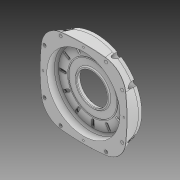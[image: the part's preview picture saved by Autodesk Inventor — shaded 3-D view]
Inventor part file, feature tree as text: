
AUTODESK INVENTOR PART (.ipt)
format: ipt  version: 2020 (Build 240168000, 168)  size: 960,000 bytes
history: native  units: mm
features: sketch x20, extrude x17, projected_geometry x5, other x4, plane x3, fillet x2, loft x1, revolve x1, pattern_circular x1, chamfer x1
ambient origin geometry x8: Origin, YZ Plane, XZ Plane, XY Plane, X Axis, Y Axis, Z Axis, Center Point
bodies: Solid1 (feature_tree)
feature tree (55):
  other  "Blocks"
  sketch  "Sketch1"  dims[d1=170.0mm d2=170.0mm]
  extrude  "Extrusion1"  Depth=170.0mm
  extrude  "Extrusion2"  Depth=60.0mm TaperAngle=0.0deg
  plane  "Work Plane1"
  loft  "Loft1"
  extrude  "Extrusion3"  Depth=7.5mm
  plane  "Work Plane2"
  sketch  "Sketch6"  dims[d14=17.5mm d15=7.5mm]
  plane  "Work Plane3"
  sketch  "Sketch7"  dims[d16=10.0mm d17=65.0mm]
  extrude  "Extrusion4"  Depth=7.5mm
  extrude  "Extrusion5"  Depth=7.5mm
  extrude  "Extrusion9"  Depth=10.0mm
  sketch  "Sketch13"  dims[d23=0.0mm d24=90.0deg d25=5.0mm d26=0.0mm]
  extrude  "Extrusion10"  Depth=7.5mm
  extrude  "Extrusion11"  TaperAngle=0.0deg  [1 undecoded]
  extrude  "Extrusion12"  Depth=5.0mm TaperAngle=0.0deg
  revolve  "Revolution1"  [1 undecoded]
  extrude  "Extrusion13"  Depth=4.0mm
  extrude  "Extrusion14"  Depth=10.0mm
  extrude  "Extrusion15"  Depth=6.0mm TaperAngle=0.0deg
  fillet  "Fillet1"  Radius=6.0mm
  extrude  "Extrusion16"  Depth=47.0mm
  fillet  "Fillet3"  Radius=60.0mm
  pattern_circular  "Circular Pattern1"  Count=6  [1 undecoded]
  extrude  "Extrusion17"  Depth=42.0mm
  extrude  "Extrusion18"  Depth=40.0mm
  extrude  "Extrusion19"  Depth=6.0mm
  extrude  "Extrusion20"  Depth=6.0mm TaperAngle=0.0deg
  chamfer  "Chamfer1"  Distance=7.0mm
  sketch  "Sketch2"  dims[d3=40.0mm d4=60.0mm d5=0.0mm]
  other  "Block1"
  sketch  "Sketch3"  dims[d7=0.0mm d8=0.0mm d9=5.5mm]
  sketch  "Sketch4"  dims[d10=57.5mm d11=7.5mm]
  projected_geometry  "Projected Loop1"
  sketch  "Sketch5"  dims[d12=7.5mm d13=7.5mm]
  projected_geometry  "Projected Loop2"
  projected_geometry  "Projected Loop3"
  projected_geometry  "Projected Loop4"
  sketch  "Sketch8"  dims[d18=7.5mm d19=7.5mm]
  sketch  "Sketch12"  dims[d20=25.0mm d21=0.0mm d22=90.0deg]
  projected_geometry  "Projected Loop5"
  sketch  "Sketch14"  dims[d27=180.0mm d28=-3.0mm]
  sketch  "Sketch15"  dims[d29=2.5mm d30=4.0mm]
  sketch  "Sketch16"  dims[d31=10.0mm d32=0.0mm d33=145.0mm]
  sketch  "Sketch17"  dims[d34=48.25mm d35=0.0mm d54=60.0mm d55=0.0mm d56=6.0mm d57=0.0mm]
  sketch  "Sketch18"  dims[d58=47.0mm d59=47.0mm d60=60.0mm d61=60.0mm]
  sketch  "Sketch19"  dims[d62=42.0mm d63=42.0mm]
  sketch  "Sketch20"  dims[d64=5.5mm d65=40.0mm]
  sketch  "Sketch21"  dims[d66=6.0mm d67=0.0mm d68=22.1mm]
  sketch  "Sketch22"  dims[d69=16.0mm d70=6.0mm d71=0.0mm]
  sketch  "Sketch23"  dims[d74=25.0mm d78=7.0mm d81=90.0deg d82=59.39697mm d83=10.0mm d85=6.2mm d86=9.0mm d87=40.0mm d89=360.0deg d91=48.25mm d92=0.0mm d93=9.0mm d94=40.0mm d96=360.0deg d98=20.0mm d99=0.0mm d100=0.0mm d101=0.0mm d104=45.0deg d105=32.6mm d107=2.0mm d108=7.0mm d109=35.0mm d110=2.0mm d111=135.0deg d112=8.0mm d113=4.0mm d115=60.0mm d116=2.5mm d117=10.0mm d118=10.0mm d119=0.0mm d120=120.0mm d121=360.0deg d123=4.0mm d124=80.0mm d125=3.3mm d126=40.0mm d128=360.0deg d130=0.0mm d131=0.0mm d133=5.7mm d134=40.0mm d136=360.0deg d138=6.0mm d139=0.0mm d140=95.5mm d141=2.0mm d142=0.8mm d143=0.0mm d144=95.5mm d145=69.5mm d146=0.8mm d147=0.0mm d148=32.0mm d149=0.5mm d150=2.0mm d151=45.0deg]
  other  "Block1:1"
  other  "Block1:2"
note: 3 required parameter values undecoded (feature->parameter linkage not recoverable at this tier; creation-order binding heuristic only, values carry confidence <= 0.55)